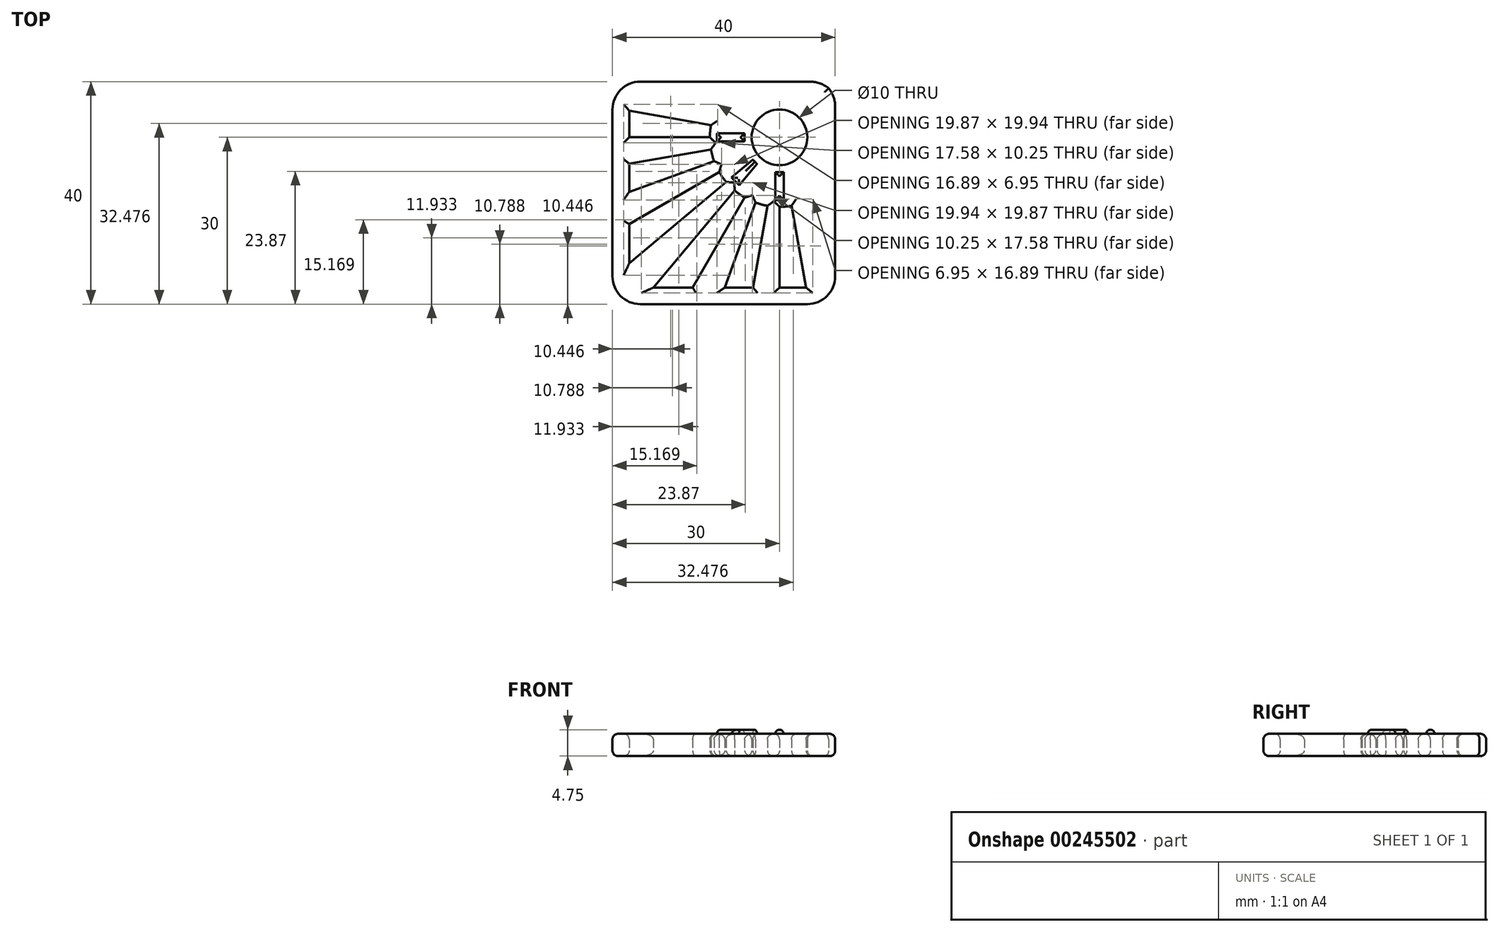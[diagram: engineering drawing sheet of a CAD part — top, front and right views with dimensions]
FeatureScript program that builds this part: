
annotation { "Feature Type Name" : "Feature", "Feature Type Description" : "" }
export const myFeature = defineFeature(function(context is Context, id is Id, definition is map)
    precondition{}
    {
        {
            var Q0;
            Q0=qCreatedBy(makeId("Top.planeOp"),FACE);
            var sketch = newSketch(context, id + "F0", { "sketchPlane" : qUnion([Q0])});
            skLineSegment(sketch, "E0.bottom", {"start": v(0, 0) * mm, "end": v(-40, 0) * mm});
            skLineSegment(sketch, "E0.top", {"start": v(0, -40) * mm, "end": v(-40, -40) * mm});
            skLineSegment(sketch, "E0.left", {"start": v(0, 0) * mm, "end": v(0, -40) * mm});
            skLineSegment(sketch, "E0.right", {"start": v(-40, 0) * mm, "end": v(-40, -40) * mm});
            skPoint(sketch, "E1", {"position": v(-10, -10) * mm});
            skLineSegment(sketch, "E2", {"start": v(-10, -10) * mm, "end": v(-35, -10) * mm});
            skLineSegment(sketch, "E3", {"start": v(-10, -10) * mm, "end": v(-34.62, -5.66) * mm});
            skLineSegment(sketch, "E4", {"start": v(-10, -10) * mm, "end": v(-5.66, -34.62) * mm});
            skLineSegment(sketch, "E5", {"start": v(-10, -10) * mm, "end": v(-10, -35) * mm});
            skLineSegment(sketch, "E6", {"start": v(-10, -10) * mm, "end": v(-34.62, -14.34) * mm});
            skLineSegment(sketch, "E7", {"start": v(-10, -10) * mm, "end": v(-33.5, -18.55) * mm});
            skLineSegment(sketch, "E8", {"start": v(-10, -10) * mm, "end": v(-31.65, -22.5) * mm});
            skLineSegment(sketch, "E9", {"start": v(-10, -10) * mm, "end": v(-29.15, -26.07) * mm});
            skLineSegment(sketch, "E10", {"start": v(-10, -10) * mm, "end": v(-26.07, -29.15) * mm});
            skLineSegment(sketch, "E11", {"start": v(-10, -10) * mm, "end": v(-22.5, -31.65) * mm});
            skLineSegment(sketch, "E12", {"start": v(-10, -10) * mm, "end": v(-18.55, -33.5) * mm});
            skLineSegment(sketch, "E13", {"start": v(-10, -10) * mm, "end": v(-14.34, -34.62) * mm});
            skCircle(sketch, "E14", {"center": v(-10, -10) * mm, "radius": 5 * mm});
            skCircle(sketch, "E15", {"center": v(-10, -10) * mm, "radius": 12.5 * mm});
            skLineSegment(sketch, "E16", {"start": v(-37, -5.24) * mm, "end": v(-37, -37) * mm});
            skLineSegment(sketch, "E17", {"start": v(-37, -37) * mm, "end": v(-5.24, -37) * mm});
            skLineSegment(sketch, "E18", {"start": v(-34.62, -5.66) * mm, "end": v(-37, -5.24) * mm});
            skLineSegment(sketch, "E19", {"start": v(-35, -10) * mm, "end": v(-37, -10) * mm});
            skLineSegment(sketch, "E20", {"start": v(-34.62, -14.34) * mm, "end": v(-37, -14.76) * mm});
            skLineSegment(sketch, "E21", {"start": v(-33.5, -18.55) * mm, "end": v(-37, -19.83) * mm});
            skLineSegment(sketch, "E22", {"start": v(-31.65, -22.5) * mm, "end": v(-37, -25.59) * mm});
            skLineSegment(sketch, "E23", {"start": v(-29.15, -26.07) * mm, "end": v(-37, -32.66) * mm});
            skLineSegment(sketch, "E24", {"start": v(-26.07, -29.15) * mm, "end": v(-32.66, -37) * mm});
            skLineSegment(sketch, "E25", {"start": v(-22.5, -31.65) * mm, "end": v(-25.59, -37) * mm});
            skLineSegment(sketch, "E26", {"start": v(-18.55, -33.5) * mm, "end": v(-19.83, -37) * mm});
            skLineSegment(sketch, "E27", {"start": v(-14.34, -34.62) * mm, "end": v(-14.76, -37) * mm});
            skLineSegment(sketch, "E28", {"start": v(-10, -35) * mm, "end": v(-10, -37) * mm});
            skLineSegment(sketch, "E29", {"start": v(-5.66, -34.62) * mm, "end": v(-5.24, -37) * mm});
            skSolve(sketch);
        }
        {
            var Q0;
            {var subQ0=sQuery(id+"F0.wireOp",EDGE,"E14");var subQ1=sQuery(id+"F0.wireOp",EDGE,"E3");var subQ2=makeQuery(id+"F0.imprint","INTERSECT",VERTEX,{"derivedFrom":[subQ1,subQ0]});Q0=makeQuery(id+"F0.imprint","IMPRINT",FACE,{"disambiguationData":[TD([[makeQuery(id+"F0.imprint","IMPRINT",EDGE,{"disambiguationData":[TD([[subQ2,-1.0]])],"derivedFrom":subQ1}),-1.0]])]});}
            var Q1;
            {var subQ0=sQuery(id+"F0.wireOp",EDGE,"E14");var subQ1=sQuery(id+"F0.wireOp",EDGE,"E4");var subQ2=makeQuery(id+"F0.imprint","INTERSECT",VERTEX,{"derivedFrom":[subQ1,subQ0]});Q1=makeQuery(id+"F0.imprint","IMPRINT",FACE,{"disambiguationData":[TD([[makeQuery(id+"F0.imprint","IMPRINT",EDGE,{"disambiguationData":[TD([[subQ2,-1.0]])],"derivedFrom":subQ1}),-1.0]])]});}
            var Q2;
            {var subQ0=sQuery(id+"F0.wireOp",EDGE,"E14");var subQ1=sQuery(id+"F0.wireOp",EDGE,"E5");var subQ2=makeQuery(id+"F0.imprint","INTERSECT",VERTEX,{"derivedFrom":[subQ1,subQ0]});Q2=makeQuery(id+"F0.imprint","IMPRINT",FACE,{"disambiguationData":[TD([[makeQuery(id+"F0.imprint","IMPRINT",EDGE,{"disambiguationData":[TD([[subQ2,-1.0]])],"derivedFrom":subQ1}),-1.0]])]});}
            var Q3;
            {var subQ0=sQuery(id+"F0.wireOp",EDGE,"E5");var subQ1=sQuery(id+"F0.wireOp",EDGE,"7b7e5d17-fbf7-4574-848a-6fc9f2fd8215.0");var subQ2=makeQuery(id+"F0.imprint","INTERSECT",VERTEX,{"derivedFrom":[subQ1,subQ0]});Q3=makeQuery(id+"F0.imprint","IMPRINT",FACE,{"disambiguationData":[TD([[makeQuery(id+"F0.imprint","IMPRINT",EDGE,{"disambiguationData":[TD([[subQ2,1.0]])],"derivedFrom":subQ1}),1.0]])]});}
            var Q4;
            {var subQ0=sQuery(id+"F0.wireOp",EDGE,"E11");var subQ1=sQuery(id+"F0.wireOp",EDGE,"7b7e5d17-fbf7-4574-848a-6fc9f2fd8215.0");var subQ2=makeQuery(id+"F0.imprint","INTERSECT",VERTEX,{"derivedFrom":[subQ1,subQ0]});Q4=makeQuery(id+"F0.imprint","IMPRINT",FACE,{"disambiguationData":[TD([[makeQuery(id+"F0.imprint","IMPRINT",EDGE,{"disambiguationData":[TD([[subQ2,-1.0]])],"derivedFrom":subQ1}),1.0]])]});}
            var Q5;
            {var subQ0=sQuery(id+"F0.wireOp",EDGE,"E9");var subQ1=sQuery(id+"F0.wireOp",EDGE,"7b7e5d17-fbf7-4574-848a-6fc9f2fd8215.0");var subQ2=makeQuery(id+"F0.imprint","INTERSECT",VERTEX,{"derivedFrom":[subQ1,subQ0]});Q5=makeQuery(id+"F0.imprint","IMPRINT",FACE,{"disambiguationData":[TD([[makeQuery(id+"F0.imprint","IMPRINT",EDGE,{"disambiguationData":[TD([[subQ2,-1.0]])],"derivedFrom":subQ1}),1.0]])]});}
            var Q6;
            {var subQ0=sQuery(id+"F0.wireOp",EDGE,"E7");var subQ1=sQuery(id+"F0.wireOp",EDGE,"7b7e5d17-fbf7-4574-848a-6fc9f2fd8215.0");var subQ2=makeQuery(id+"F0.imprint","INTERSECT",VERTEX,{"derivedFrom":[subQ1,subQ0]});Q6=makeQuery(id+"F0.imprint","IMPRINT",FACE,{"disambiguationData":[TD([[makeQuery(id+"F0.imprint","IMPRINT",EDGE,{"disambiguationData":[TD([[subQ2,-1.0]])],"derivedFrom":subQ1}),1.0]])]});}
            var Q7;
            {var subQ0=sQuery(id+"F0.wireOp",EDGE,"E2");var subQ1=sQuery(id+"F0.wireOp",EDGE,"7b7e5d17-fbf7-4574-848a-6fc9f2fd8215.0");var subQ2=makeQuery(id+"F0.imprint","INTERSECT",VERTEX,{"derivedFrom":[subQ1,subQ0]});Q7=makeQuery(id+"F0.imprint","IMPRINT",FACE,{"disambiguationData":[TD([[makeQuery(id+"F0.imprint","IMPRINT",EDGE,{"disambiguationData":[TD([[subQ2,-1.0]])],"derivedFrom":subQ1}),1.0]])]});}
            var Q8;
            {var subQ0=sQuery(id+"F0.wireOp",EDGE,"E14");var subQ1=sQuery(id+"F0.wireOp",EDGE,"E2");var subQ2=makeQuery(id+"F0.imprint","INTERSECT",VERTEX,{"derivedFrom":[subQ1,subQ0]});Q8=makeQuery(id+"F0.imprint","IMPRINT",FACE,{"disambiguationData":[TD([[makeQuery(id+"F0.imprint","IMPRINT",EDGE,{"disambiguationData":[TD([[subQ2,-1.0]])],"derivedFrom":subQ1}),-1.0]])]});}
            var Q9;
            {var subQ0=sQuery(id+"F0.wireOp",EDGE,"E14");var subQ1=sQuery(id+"F0.wireOp",EDGE,"E2");var subQ2=makeQuery(id+"F0.imprint","INTERSECT",VERTEX,{"derivedFrom":[subQ1,subQ0]});Q9=makeQuery(id+"F0.imprint","IMPRINT",FACE,{"disambiguationData":[TD([[makeQuery(id+"F0.imprint","IMPRINT",EDGE,{"disambiguationData":[TD([[subQ2,-1.0]])],"derivedFrom":subQ1}),1.0]])]});}
            var Q10;
            {var subQ0=sQuery(id+"F0.wireOp",EDGE,"E14");var subQ1=sQuery(id+"F0.wireOp",EDGE,"E6");var subQ2=makeQuery(id+"F0.imprint","INTERSECT",VERTEX,{"derivedFrom":[subQ1,subQ0]});Q10=makeQuery(id+"F0.imprint","IMPRINT",FACE,{"disambiguationData":[TD([[makeQuery(id+"F0.imprint","IMPRINT",EDGE,{"disambiguationData":[TD([[subQ2,-1.0]])],"derivedFrom":subQ1}),1.0]])]});}
            var Q11;
            {var subQ0=sQuery(id+"F0.wireOp",EDGE,"E14");var subQ1=sQuery(id+"F0.wireOp",EDGE,"E7");var subQ2=makeQuery(id+"F0.imprint","INTERSECT",VERTEX,{"derivedFrom":[subQ1,subQ0]});Q11=makeQuery(id+"F0.imprint","IMPRINT",FACE,{"disambiguationData":[TD([[makeQuery(id+"F0.imprint","IMPRINT",EDGE,{"disambiguationData":[TD([[subQ2,-1.0]])],"derivedFrom":subQ1}),1.0]])]});}
            var Q12;
            {var subQ0=sQuery(id+"F0.wireOp",EDGE,"E14");var subQ1=sQuery(id+"F0.wireOp",EDGE,"E8");var subQ2=makeQuery(id+"F0.imprint","INTERSECT",VERTEX,{"derivedFrom":[subQ1,subQ0]});Q12=makeQuery(id+"F0.imprint","IMPRINT",FACE,{"disambiguationData":[TD([[makeQuery(id+"F0.imprint","IMPRINT",EDGE,{"disambiguationData":[TD([[subQ2,-1.0]])],"derivedFrom":subQ1}),1.0]])]});}
            var Q13;
            {var subQ0=sQuery(id+"F0.wireOp",EDGE,"E14");var subQ1=sQuery(id+"F0.wireOp",EDGE,"E9");var subQ2=makeQuery(id+"F0.imprint","INTERSECT",VERTEX,{"derivedFrom":[subQ1,subQ0]});Q13=makeQuery(id+"F0.imprint","IMPRINT",FACE,{"disambiguationData":[TD([[makeQuery(id+"F0.imprint","IMPRINT",EDGE,{"disambiguationData":[TD([[subQ2,-1.0]])],"derivedFrom":subQ1}),1.0]])]});}
            var Q14;
            {var subQ0=sQuery(id+"F0.wireOp",EDGE,"E14");var subQ1=sQuery(id+"F0.wireOp",EDGE,"E10");var subQ2=makeQuery(id+"F0.imprint","INTERSECT",VERTEX,{"derivedFrom":[subQ1,subQ0]});Q14=makeQuery(id+"F0.imprint","IMPRINT",FACE,{"disambiguationData":[TD([[makeQuery(id+"F0.imprint","IMPRINT",EDGE,{"disambiguationData":[TD([[subQ2,-1.0]])],"derivedFrom":subQ1}),1.0]])]});}
            var Q15;
            {var subQ0=sQuery(id+"F0.wireOp",EDGE,"E14");var subQ1=sQuery(id+"F0.wireOp",EDGE,"E11");var subQ2=makeQuery(id+"F0.imprint","INTERSECT",VERTEX,{"derivedFrom":[subQ1,subQ0]});Q15=makeQuery(id+"F0.imprint","IMPRINT",FACE,{"disambiguationData":[TD([[makeQuery(id+"F0.imprint","IMPRINT",EDGE,{"disambiguationData":[TD([[subQ2,-1.0]])],"derivedFrom":subQ1}),1.0]])]});}
            var Q16;
            {var subQ0=sQuery(id+"F0.wireOp",EDGE,"E14");var subQ1=sQuery(id+"F0.wireOp",EDGE,"E12");var subQ2=makeQuery(id+"F0.imprint","INTERSECT",VERTEX,{"derivedFrom":[subQ1,subQ0]});Q16=makeQuery(id+"F0.imprint","IMPRINT",FACE,{"disambiguationData":[TD([[makeQuery(id+"F0.imprint","IMPRINT",EDGE,{"disambiguationData":[TD([[subQ2,-1.0]])],"derivedFrom":subQ1}),1.0]])]});}
            var Q17;
            {var subQ13=sQuery(id+"F0.wireOp",EDGE,"E0.top");Q17=makeQuery(id+"F0.imprint","IMPRINT",FACE,{"disambiguationData":[TD([[makeQuery(id+"F0.imprint","IMPRINT",EDGE,{"derivedFrom":subQ13}),-1.0]])]});}
            var Q18;
            {var subQ5=sQuery(id+"F0.wireOp",EDGE,"E27");Q18=makeQuery(id+"F0.imprint","IMPRINT",FACE,{"disambiguationData":[TD([[makeQuery(id+"F0.imprint","IMPRINT",EDGE,{"derivedFrom":subQ5}),1.0]])]});}
            var Q19;
            {var subQ4=sQuery(id+"F0.wireOp",EDGE,"E25");Q19=makeQuery(id+"F0.imprint","IMPRINT",FACE,{"disambiguationData":[TD([[makeQuery(id+"F0.imprint","IMPRINT",EDGE,{"derivedFrom":subQ4}),1.0]])]});}
            var Q20;
            {var subQ9=sQuery(id+"F0.wireOp",EDGE,"E23");Q20=makeQuery(id+"F0.imprint","IMPRINT",FACE,{"disambiguationData":[TD([[makeQuery(id+"F0.imprint","IMPRINT",EDGE,{"derivedFrom":subQ9}),1.0]])]});}
            var Q21;
            {var subQ5=sQuery(id+"F0.wireOp",EDGE,"E21");Q21=makeQuery(id+"F0.imprint","IMPRINT",FACE,{"disambiguationData":[TD([[makeQuery(id+"F0.imprint","IMPRINT",EDGE,{"derivedFrom":subQ5}),1.0]])]});}
            var Q22;
            {var subQ0=sQuery(id+"F0.wireOp",EDGE,"E19");Q22=makeQuery(id+"F0.imprint","IMPRINT",FACE,{"disambiguationData":[TD([[makeQuery(id+"F0.imprint","IMPRINT",EDGE,{"derivedFrom":subQ0}),1.0]])]});}
            extrude(context, id + "F1", {"entities" : qUnion([Q0, Q1, Q2, Q3, Q4, Q5, Q6, Q7, Q8, Q9, Q10, Q11, Q12, Q13, Q14, Q15, Q16, Q17, Q18, Q19, Q20, Q21, Q22]), "depth" : 4 * mm});
        }
        {
            var Q0;
            Q0=makeQuery(id+"F1.opExtrude","SWEPT_EDGE",EDGE,{"disambiguationData":[OSD([sQuery(id+"F0.wireOp",EDGE,"E0.bottom"),sQuery(id+"F0.wireOp",EDGE,"E0.left")])]});
            var Q1;
            Q1=makeQuery(id+"F1.opExtrude","SWEPT_EDGE",EDGE,{"disambiguationData":[OSD([sQuery(id+"F0.wireOp",EDGE,"E0.top"),sQuery(id+"F0.wireOp",EDGE,"E0.left")])]});
            var Q2;
            Q2=makeQuery(id+"F1.opExtrude","SWEPT_EDGE",EDGE,{"disambiguationData":[OSD([sQuery(id+"F0.wireOp",EDGE,"E0.bottom"),sQuery(id+"F0.wireOp",EDGE,"E0.right")])]});
            var Q3;
            Q3=makeQuery(id+"F1.opExtrude","SWEPT_EDGE",EDGE,{"disambiguationData":[OSD([sQuery(id+"F0.wireOp",EDGE,"E0.top"),sQuery(id+"F0.wireOp",EDGE,"E0.right")])]});
            fillet(context, id + "F2", {"entities" : qUnion([Q0, Q1, Q2, Q3]), "radius" : 5 * mm, "tangentPropagation" : true, "allowEdgeOverflow" : false});
        }
        {
            var Q0;
            Q0=makeQuery(id+"F1.opExtrude","CAP_FACE",FACE,{"disambiguationData":[OSD([sQuery(id+"F0.wireOp",EDGE,"E0.bottom"),sQuery(id+"F0.wireOp",EDGE,"E0.top"),sQuery(id+"F0.wireOp",EDGE,"E0.left"),sQuery(id+"F0.wireOp",EDGE,"E0.right"),sQuery(id+"F0.wireOp",EDGE,"E2"),sQuery(id+"F0.wireOp",EDGE,"E3"),sQuery(id+"F0.wireOp",EDGE,"E4"),sQuery(id+"F0.wireOp",EDGE,"E5"),sQuery(id+"F0.wireOp",EDGE,"E6"),sQuery(id+"F0.wireOp",EDGE,"E7"),sQuery(id+"F0.wireOp",EDGE,"E8"),sQuery(id+"F0.wireOp",EDGE,"E9"),sQuery(id+"F0.wireOp",EDGE,"E10"),sQuery(id+"F0.wireOp",EDGE,"E11"),sQuery(id+"F0.wireOp",EDGE,"E12"),sQuery(id+"F0.wireOp",EDGE,"E13"),sQuery(id+"F0.wireOp",EDGE,"E14"),sQuery(id+"F0.wireOp",EDGE,"E15"),sQuery(id+"F0.wireOp",EDGE,"E16"),sQuery(id+"F0.wireOp",EDGE,"E17"),sQuery(id+"F0.wireOp",EDGE,"E18"),sQuery(id+"F0.wireOp",EDGE,"E19"),sQuery(id+"F0.wireOp",EDGE,"E20"),sQuery(id+"F0.wireOp",EDGE,"E21"),sQuery(id+"F0.wireOp",EDGE,"E22"),sQuery(id+"F0.wireOp",EDGE,"E23"),sQuery(id+"F0.wireOp",EDGE,"E24"),sQuery(id+"F0.wireOp",EDGE,"E25"),sQuery(id+"F0.wireOp",EDGE,"E26"),sQuery(id+"F0.wireOp",EDGE,"E27"),sQuery(id+"F0.wireOp",EDGE,"E28"),sQuery(id+"F0.wireOp",EDGE,"E29")])],"isStart":false});
            var sketch = newSketch(context, id + "F3", { "sketchPlane" : qUnion([Q0])});
            skLineSegment(sketch, "E30", {"start": v(-10, -22.5) * mm, "end": v(-10, -15) * mm});
            skLineSegment(sketch, "E31", {"start": v(-22.5, -10) * mm, "end": v(-15, -10) * mm});
            skLineSegment(sketch, "E32.bottom", {"start": v(-9.25, -21.25) * mm, "end": v(-10.75, -21.25) * mm});
            skLineSegment(sketch, "E32.top", {"start": v(-9.25, -16.25) * mm, "end": v(-10.75, -16.25) * mm});
            skLineSegment(sketch, "E32.left", {"start": v(-9.25, -21.25) * mm, "end": v(-9.25, -16.25) * mm});
            skLineSegment(sketch, "E32.right", {"start": v(-10.75, -21.25) * mm, "end": v(-10.75, -16.25) * mm});
            skPoint(sketch, "E32.middle", {"position": v(-10, -18.75) * mm});
            skLineSegment(sketch, "E33.bottom", {"start": v(-16.25, -10.75) * mm, "end": v(-21.25, -10.75) * mm});
            skLineSegment(sketch, "E33.top", {"start": v(-16.25, -9.25) * mm, "end": v(-21.25, -9.25) * mm});
            skLineSegment(sketch, "E33.left", {"start": v(-16.25, -10.75) * mm, "end": v(-16.25, -9.25) * mm});
            skLineSegment(sketch, "E33.right", {"start": v(-21.25, -10.75) * mm, "end": v(-21.25, -9.25) * mm});
            skPoint(sketch, "E33.middle", {"position": v(-18.75, -10) * mm});
            skLineSegment(sketch, "E34", {"start": v(-19.58, -18.03) * mm, "end": v(-13.83, -13.21) * mm});
            skLineSegment(sketch, "E35", {"start": v(-19.58, -18.03) * mm, "end": v(-18.03, -19.58) * mm});
            skLineSegment(sketch, "E36", {"start": v(-18.03, -19.58) * mm, "end": v(-13.21, -13.83) * mm});
            skLineSegment(sketch, "E37", {"start": v(-14.79, -14.02) * mm, "end": v(-14.02, -14.79) * mm});
            skLineSegment(sketch, "E38", {"start": v(-18.62, -17.23) * mm, "end": v(-17.23, -18.62) * mm});
            skSolve(sketch);
        }
        {
            var Q0;
            {var subQ0=sQuery(id+"F3.wireOp",EDGE,"E37");Q0=makeQuery(id+"F3.imprint","IMPRINT",FACE,{"disambiguationData":[TD([[makeQuery(id+"F3.imprint","IMPRINT",EDGE,{"derivedFrom":subQ0}),-1.0]])]});}
            var Q1;
            {var subQ5=sQuery(id+"F3.wireOp",EDGE,"E32.right");Q1=makeQuery(id+"F3.imprint","IMPRINT",FACE,{"disambiguationData":[TD([[makeQuery(id+"F3.imprint","IMPRINT",EDGE,{"derivedFrom":subQ5}),-1.0]])]});}
            var Q2;
            {var subQ5=sQuery(id+"F3.wireOp",EDGE,"E32.left");Q2=makeQuery(id+"F3.imprint","IMPRINT",FACE,{"disambiguationData":[TD([[makeQuery(id+"F3.imprint","IMPRINT",EDGE,{"derivedFrom":subQ5}),1.0]])]});}
            var Q3;
            {var subQ5=sQuery(id+"F3.wireOp",EDGE,"E33.bottom");Q3=makeQuery(id+"F3.imprint","IMPRINT",FACE,{"disambiguationData":[TD([[makeQuery(id+"F3.imprint","IMPRINT",EDGE,{"derivedFrom":subQ5}),-1.0]])]});}
            var Q4;
            {var subQ5=sQuery(id+"F3.wireOp",EDGE,"E33.top");Q4=makeQuery(id+"F3.imprint","IMPRINT",FACE,{"disambiguationData":[TD([[makeQuery(id+"F3.imprint","IMPRINT",EDGE,{"derivedFrom":subQ5}),1.0]])]});}
            extrude(context, id + "F4", {"entities" : qUnion([Q0, Q1, Q2, Q3, Q4]), "operationType" : NewBodyOperationType.ADD, "depth" : 0.75 * mm});
        }
        {
            var Q0;
            Q0=makeQuery(id+"F4.opExtrude","CAP_EDGE",EDGE,{"disambiguationData":[OSD([sQuery(id+"F3.wireOp",EDGE,"E32.left")])],"isStart":false});
            var Q1;
            Q1=makeQuery(id+"F4.opExtrude","CAP_EDGE",EDGE,{"disambiguationData":[OSD([sQuery(id+"F3.wireOp",EDGE,"E32.right")])],"isStart":false});
            var Q2;
            Q2=makeQuery(id+"F4.opExtrude","CAP_EDGE",EDGE,{"disambiguationData":[OSD([sQuery(id+"F3.wireOp",EDGE,"E36")])],"isStart":false});
            var Q3;
            Q3=makeQuery(id+"F4.opExtrude","CAP_EDGE",EDGE,{"disambiguationData":[OSD([sQuery(id+"F3.wireOp",EDGE,"E34")])],"isStart":false});
            var Q4;
            Q4=makeQuery(id+"F4.opExtrude","CAP_EDGE",EDGE,{"disambiguationData":[OSD([sQuery(id+"F3.wireOp",EDGE,"E33.bottom")])],"isStart":false});
            var Q5;
            Q5=makeQuery(id+"F4.opExtrude","CAP_EDGE",EDGE,{"disambiguationData":[OSD([sQuery(id+"F3.wireOp",EDGE,"E33.top")])],"isStart":false});
            var Q6;
            Q6=makeQuery(id+"F4.opExtrude","CAP_EDGE",EDGE,{"disambiguationData":[OSD([sQuery(id+"F3.wireOp",EDGE,"E38")])],"isStart":false});
            var Q7;
            Q7=makeQuery(id+"F4.opExtrude","CAP_EDGE",EDGE,{"disambiguationData":[OSD([sQuery(id+"F3.wireOp",EDGE,"E32.bottom")])],"isStart":false});
            var Q8;
            Q8=makeQuery(id+"F4.opExtrude","CAP_EDGE",EDGE,{"disambiguationData":[OSD([sQuery(id+"F3.wireOp",EDGE,"E33.right")])],"isStart":false});
            var Q9;
            Q9=makeQuery(id+"F4.opExtrude","CAP_EDGE",EDGE,{"disambiguationData":[OSD([sQuery(id+"F3.wireOp",EDGE,"E33.left")])],"isStart":false});
            var Q10;
            Q10=makeQuery(id+"F4.opExtrude","CAP_EDGE",EDGE,{"disambiguationData":[OSD([sQuery(id+"F3.wireOp",EDGE,"E37")])],"isStart":false});
            var Q11;
            Q11=makeQuery(id+"F4.opExtrude","CAP_EDGE",EDGE,{"disambiguationData":[OSD([sQuery(id+"F3.wireOp",EDGE,"E32.top")])],"isStart":false});
            fillet(context, id + "F5", {"entities" : qUnion([Q0, Q1, Q2, Q3, Q4, Q5, Q6, Q7, Q8, Q9, Q10, Q11]), "radius" : 0.75 * mm, "tangentPropagation" : true, "allowEdgeOverflow" : false});
        }
        {
            var Q0;
            Q0=makeQuery(id+"F1.opExtrude","CAP_EDGE",EDGE,{"disambiguationData":[OSD([sQuery(id+"F0.wireOp",EDGE,"E4"),sQuery(id+"F0.wireOp",EDGE,"E29")])],"isStart":false});
            var Q1;
            {var subQ0=sQuery(id+"F0.wireOp",EDGE,"E15");Q1=makeQuery(id+"F1.opExtrude","CAP_EDGE",EDGE,{"disambiguationData":[OSD([subQ0]),TDD([makeQuery(id+"F0.imprint","IMPRINT",EDGE,{"disambiguationData":[TD([[makeQuery(id+"F0.imprint","INTERSECT",VERTEX,{"derivedFrom":[sQuery(id+"F0.wireOp",EDGE,"E4"),subQ0]}),1.0]])],"derivedFrom":subQ0})])],"isStart":false});}
            var Q2;
            Q2=makeQuery(id+"F1.opExtrude","CAP_EDGE",EDGE,{"disambiguationData":[OSD([sQuery(id+"F0.wireOp",EDGE,"E5"),sQuery(id+"F0.wireOp",EDGE,"E28")])],"isStart":false});
            var Q3;
            {var subQ0=sQuery(id+"F0.wireOp",EDGE,"E17");Q3=makeQuery(id+"F1.opExtrude","CAP_EDGE",EDGE,{"disambiguationData":[OSD([subQ0]),TDD([makeQuery(id+"F0.imprint","IMPRINT",EDGE,{"disambiguationData":[TD([[makeQuery(id+"F0.imprint","INTERSECT",VERTEX,{"derivedFrom":[subQ0,sQuery(id+"F0.wireOp",EDGE,"E29")]}),1.0]])],"derivedFrom":subQ0})])],"isStart":false});}
            var Q4;
            Q4=makeQuery(id+"F1.opExtrude","CAP_EDGE",EDGE,{"disambiguationData":[OSD([sQuery(id+"F0.wireOp",EDGE,"E13"),sQuery(id+"F0.wireOp",EDGE,"E27")])],"isStart":false});
            var Q5;
            {var subQ0=sQuery(id+"F0.wireOp",EDGE,"E17");Q5=makeQuery(id+"F1.opExtrude","CAP_EDGE",EDGE,{"disambiguationData":[OSD([subQ0]),TDD([makeQuery(id+"F0.imprint","IMPRINT",EDGE,{"disambiguationData":[TD([[makeQuery(id+"F0.imprint","INTERSECT",VERTEX,{"derivedFrom":[subQ0,sQuery(id+"F0.wireOp",EDGE,"E26")]}),-1.0]])],"derivedFrom":subQ0})])],"isStart":false});}
            var Q6;
            Q6=makeQuery(id+"F1.opExtrude","CAP_EDGE",EDGE,{"disambiguationData":[OSD([sQuery(id+"F0.wireOp",EDGE,"E12"),sQuery(id+"F0.wireOp",EDGE,"E26")])],"isStart":false});
            var Q7;
            {var subQ0=sQuery(id+"F0.wireOp",EDGE,"E15");Q7=makeQuery(id+"F1.opExtrude","CAP_EDGE",EDGE,{"disambiguationData":[OSD([subQ0]),TDD([makeQuery(id+"F0.imprint","IMPRINT",EDGE,{"disambiguationData":[TD([[makeQuery(id+"F0.imprint","INTERSECT",VERTEX,{"derivedFrom":[sQuery(id+"F0.wireOp",EDGE,"E12"),subQ0]}),-1.0]])],"derivedFrom":subQ0})])],"isStart":false});}
            var Q8;
            Q8=makeQuery(id+"F1.opExtrude","CAP_EDGE",EDGE,{"disambiguationData":[OSD([sQuery(id+"F0.wireOp",EDGE,"E11"),sQuery(id+"F0.wireOp",EDGE,"E25")])],"isStart":false});
            var Q9;
            {var subQ0=sQuery(id+"F0.wireOp",EDGE,"E15");Q9=makeQuery(id+"F1.opExtrude","CAP_EDGE",EDGE,{"disambiguationData":[OSD([subQ0]),TDD([makeQuery(id+"F0.imprint","IMPRINT",EDGE,{"disambiguationData":[TD([[makeQuery(id+"F0.imprint","INTERSECT",VERTEX,{"derivedFrom":[sQuery(id+"F0.wireOp",EDGE,"E10"),subQ0]}),-1.0]])],"derivedFrom":subQ0})])],"isStart":false});}
            var Q10;
            Q10=makeQuery(id+"F1.opExtrude","CAP_EDGE",EDGE,{"disambiguationData":[OSD([sQuery(id+"F0.wireOp",EDGE,"E3"),sQuery(id+"F0.wireOp",EDGE,"E18")])],"isStart":false});
            var Q11;
            {var subQ0=sQuery(id+"F0.wireOp",EDGE,"E16");Q11=makeQuery(id+"F1.opExtrude","CAP_EDGE",EDGE,{"disambiguationData":[OSD([subQ0]),TDD([makeQuery(id+"F0.imprint","IMPRINT",EDGE,{"disambiguationData":[TD([[makeQuery(id+"F0.imprint","INTERSECT",VERTEX,{"derivedFrom":[subQ0,sQuery(id+"F0.wireOp",EDGE,"E18")]}),-1.0]])],"derivedFrom":subQ0})])],"isStart":false});}
            var Q12;
            {var subQ0=sQuery(id+"F0.wireOp",EDGE,"E16");Q12=makeQuery(id+"F1.opExtrude","CAP_EDGE",EDGE,{"disambiguationData":[OSD([subQ0]),TDD([makeQuery(id+"F0.imprint","IMPRINT",EDGE,{"disambiguationData":[TD([[makeQuery(id+"F0.imprint","INTERSECT",VERTEX,{"derivedFrom":[subQ0,sQuery(id+"F0.wireOp",EDGE,"E20")]}),-1.0]])],"derivedFrom":subQ0})])],"isStart":false});}
            var Q13;
            Q13=makeQuery(id+"F1.opExtrude","CAP_EDGE",EDGE,{"disambiguationData":[OSD([sQuery(id+"F0.wireOp",EDGE,"E2"),sQuery(id+"F0.wireOp",EDGE,"E19")])],"isStart":false});
            var Q14;
            Q14=makeQuery(id+"F1.opExtrude","CAP_EDGE",EDGE,{"disambiguationData":[OSD([sQuery(id+"F0.wireOp",EDGE,"E6"),sQuery(id+"F0.wireOp",EDGE,"E20")])],"isStart":false});
            var Q15;
            {var subQ0=sQuery(id+"F0.wireOp",EDGE,"E15");Q15=makeQuery(id+"F1.opExtrude","CAP_EDGE",EDGE,{"disambiguationData":[OSD([subQ0]),TDD([makeQuery(id+"F0.imprint","IMPRINT",EDGE,{"disambiguationData":[TD([[makeQuery(id+"F0.imprint","INTERSECT",VERTEX,{"derivedFrom":[sQuery(id+"F0.wireOp",EDGE,"E2"),subQ0]}),1.0]])],"derivedFrom":subQ0})])],"isStart":false});}
            var Q16;
            {var subQ0=sQuery(id+"F0.wireOp",EDGE,"E15");Q16=makeQuery(id+"F1.opExtrude","CAP_EDGE",EDGE,{"disambiguationData":[OSD([subQ0]),TDD([makeQuery(id+"F0.imprint","IMPRINT",EDGE,{"disambiguationData":[TD([[makeQuery(id+"F0.imprint","INTERSECT",VERTEX,{"derivedFrom":[sQuery(id+"F0.wireOp",EDGE,"E6"),subQ0]}),-1.0]])],"derivedFrom":subQ0})])],"isStart":false});}
            var Q17;
            Q17=makeQuery(id+"F1.opExtrude","CAP_EDGE",EDGE,{"disambiguationData":[OSD([sQuery(id+"F0.wireOp",EDGE,"E7"),sQuery(id+"F0.wireOp",EDGE,"E21")])],"isStart":false});
            var Q18;
            Q18=makeQuery(id+"F1.opExtrude","CAP_EDGE",EDGE,{"disambiguationData":[OSD([sQuery(id+"F0.wireOp",EDGE,"E8"),sQuery(id+"F0.wireOp",EDGE,"E22")])],"isStart":false});
            var Q19;
            {var subQ0=sQuery(id+"F0.wireOp",EDGE,"E15");Q19=makeQuery(id+"F1.opExtrude","CAP_EDGE",EDGE,{"disambiguationData":[OSD([subQ0]),TDD([makeQuery(id+"F0.imprint","IMPRINT",EDGE,{"disambiguationData":[TD([[makeQuery(id+"F0.imprint","INTERSECT",VERTEX,{"derivedFrom":[sQuery(id+"F0.wireOp",EDGE,"E8"),subQ0]}),-1.0]])],"derivedFrom":subQ0})])],"isStart":false});}
            var Q20;
            {var subQ0=sQuery(id+"F0.wireOp",EDGE,"E16");Q20=makeQuery(id+"F1.opExtrude","CAP_EDGE",EDGE,{"disambiguationData":[OSD([subQ0]),TDD([makeQuery(id+"F0.imprint","IMPRINT",EDGE,{"disambiguationData":[TD([[makeQuery(id+"F0.imprint","INTERSECT",VERTEX,{"derivedFrom":[subQ0,sQuery(id+"F0.wireOp",EDGE,"E22")]}),-1.0]])],"derivedFrom":subQ0})])],"isStart":false});}
            var Q21;
            {var subQ0=sQuery(id+"F0.wireOp",EDGE,"E17");Q21=makeQuery(id+"F1.opExtrude","CAP_EDGE",EDGE,{"disambiguationData":[OSD([subQ0]),TDD([makeQuery(id+"F0.imprint","IMPRINT",EDGE,{"disambiguationData":[TD([[makeQuery(id+"F0.imprint","INTERSECT",VERTEX,{"derivedFrom":[subQ0,sQuery(id+"F0.wireOp",EDGE,"E24")]}),-1.0]])],"derivedFrom":subQ0})])],"isStart":false});}
            var Q22;
            Q22=makeQuery(id+"F1.opExtrude","CAP_EDGE",EDGE,{"disambiguationData":[OSD([sQuery(id+"F0.wireOp",EDGE,"E10"),sQuery(id+"F0.wireOp",EDGE,"E24")])],"isStart":false});
            var Q23;
            Q23=makeQuery(id+"F1.opExtrude","CAP_EDGE",EDGE,{"disambiguationData":[OSD([sQuery(id+"F0.wireOp",EDGE,"E9"),sQuery(id+"F0.wireOp",EDGE,"E23")])],"isStart":false});
            var Q24;
            Q24=makeQuery(id+"F1.opExtrude","CAP_EDGE",EDGE,{"disambiguationData":[OSD([sQuery(id+"F0.wireOp",EDGE,"E14")])],"isStart":false});
            var Q25;
            Q25=makeQuery(id+"F1.opExtrude","CAP_EDGE",EDGE,{"disambiguationData":[OSD([sQuery(id+"F0.wireOp",EDGE,"E0.right")])],"isStart":false});
            var Q26;
            Q26=makeQuery(id+"F1.opExtrude","CAP_EDGE",EDGE,{"disambiguationData":[OSD([sQuery(id+"F0.wireOp",EDGE,"E14")])],"isStart":true});
            var Q27;
            Q27=makeQuery(id+"F1.opExtrude","CAP_EDGE",EDGE,{"disambiguationData":[OSD([sQuery(id+"F0.wireOp",EDGE,"E0.left")])],"isStart":true});
            var Q28;
            Q28=makeQuery(id+"F1.opExtrude","CAP_EDGE",EDGE,{"disambiguationData":[OSD([sQuery(id+"F0.wireOp",EDGE,"E3"),sQuery(id+"F0.wireOp",EDGE,"E18")])],"isStart":true});
            var Q29;
            {var subQ0=sQuery(id+"F0.wireOp",EDGE,"E15");Q29=makeQuery(id+"F1.opExtrude","CAP_EDGE",EDGE,{"disambiguationData":[OSD([subQ0]),TDD([makeQuery(id+"F0.imprint","IMPRINT",EDGE,{"disambiguationData":[TD([[makeQuery(id+"F0.imprint","INTERSECT",VERTEX,{"derivedFrom":[sQuery(id+"F0.wireOp",EDGE,"E2"),subQ0]}),1.0]])],"derivedFrom":subQ0})])],"isStart":true});}
            var Q30;
            {var subQ0=sQuery(id+"F0.wireOp",EDGE,"E16");Q30=makeQuery(id+"F1.opExtrude","CAP_EDGE",EDGE,{"disambiguationData":[OSD([subQ0]),TDD([makeQuery(id+"F0.imprint","IMPRINT",EDGE,{"disambiguationData":[TD([[makeQuery(id+"F0.imprint","INTERSECT",VERTEX,{"derivedFrom":[subQ0,sQuery(id+"F0.wireOp",EDGE,"E18")]}),-1.0]])],"derivedFrom":subQ0})])],"isStart":true});}
            var Q31;
            Q31=makeQuery(id+"F1.opExtrude","CAP_EDGE",EDGE,{"disambiguationData":[OSD([sQuery(id+"F0.wireOp",EDGE,"E2"),sQuery(id+"F0.wireOp",EDGE,"E19")])],"isStart":true});
            var Q32;
            Q32=makeQuery(id+"F1.opExtrude","CAP_EDGE",EDGE,{"disambiguationData":[OSD([sQuery(id+"F0.wireOp",EDGE,"E6"),sQuery(id+"F0.wireOp",EDGE,"E20")])],"isStart":true});
            var Q33;
            {var subQ0=sQuery(id+"F0.wireOp",EDGE,"E16");Q33=makeQuery(id+"F1.opExtrude","CAP_EDGE",EDGE,{"disambiguationData":[OSD([subQ0]),TDD([makeQuery(id+"F0.imprint","IMPRINT",EDGE,{"disambiguationData":[TD([[makeQuery(id+"F0.imprint","INTERSECT",VERTEX,{"derivedFrom":[subQ0,sQuery(id+"F0.wireOp",EDGE,"E20")]}),-1.0]])],"derivedFrom":subQ0})])],"isStart":true});}
            var Q34;
            Q34=makeQuery(id+"F1.opExtrude","CAP_EDGE",EDGE,{"disambiguationData":[OSD([sQuery(id+"F0.wireOp",EDGE,"E7"),sQuery(id+"F0.wireOp",EDGE,"E21")])],"isStart":true});
            var Q35;
            {var subQ0=sQuery(id+"F0.wireOp",EDGE,"E15");Q35=makeQuery(id+"F1.opExtrude","CAP_EDGE",EDGE,{"disambiguationData":[OSD([subQ0]),TDD([makeQuery(id+"F0.imprint","IMPRINT",EDGE,{"disambiguationData":[TD([[makeQuery(id+"F0.imprint","INTERSECT",VERTEX,{"derivedFrom":[sQuery(id+"F0.wireOp",EDGE,"E6"),subQ0]}),-1.0]])],"derivedFrom":subQ0})])],"isStart":true});}
            var Q36;
            Q36=makeQuery(id+"F1.opExtrude","CAP_EDGE",EDGE,{"disambiguationData":[OSD([sQuery(id+"F0.wireOp",EDGE,"E8"),sQuery(id+"F0.wireOp",EDGE,"E22")])],"isStart":true});
            var Q37;
            {var subQ0=sQuery(id+"F0.wireOp",EDGE,"E15");Q37=makeQuery(id+"F1.opExtrude","CAP_EDGE",EDGE,{"disambiguationData":[OSD([subQ0]),TDD([makeQuery(id+"F0.imprint","IMPRINT",EDGE,{"disambiguationData":[TD([[makeQuery(id+"F0.imprint","INTERSECT",VERTEX,{"derivedFrom":[sQuery(id+"F0.wireOp",EDGE,"E8"),subQ0]}),-1.0]])],"derivedFrom":subQ0})])],"isStart":true});}
            var Q38;
            Q38=makeQuery(id+"F1.opExtrude","CAP_EDGE",EDGE,{"disambiguationData":[OSD([sQuery(id+"F0.wireOp",EDGE,"E9"),sQuery(id+"F0.wireOp",EDGE,"E23")])],"isStart":true});
            var Q39;
            {var subQ0=sQuery(id+"F0.wireOp",EDGE,"E15");Q39=makeQuery(id+"F1.opExtrude","CAP_EDGE",EDGE,{"disambiguationData":[OSD([subQ0]),TDD([makeQuery(id+"F0.imprint","IMPRINT",EDGE,{"disambiguationData":[TD([[makeQuery(id+"F0.imprint","INTERSECT",VERTEX,{"derivedFrom":[sQuery(id+"F0.wireOp",EDGE,"E10"),subQ0]}),-1.0]])],"derivedFrom":subQ0})])],"isStart":true});}
            var Q40;
            Q40=makeQuery(id+"F1.opExtrude","CAP_EDGE",EDGE,{"disambiguationData":[OSD([sQuery(id+"F0.wireOp",EDGE,"E10"),sQuery(id+"F0.wireOp",EDGE,"E24")])],"isStart":true});
            var Q41;
            Q41=makeQuery(id+"F1.opExtrude","CAP_EDGE",EDGE,{"disambiguationData":[OSD([sQuery(id+"F0.wireOp",EDGE,"E11"),sQuery(id+"F0.wireOp",EDGE,"E25")])],"isStart":true});
            var Q42;
            {var subQ0=sQuery(id+"F0.wireOp",EDGE,"E16");Q42=makeQuery(id+"F1.opExtrude","CAP_EDGE",EDGE,{"disambiguationData":[OSD([subQ0]),TDD([makeQuery(id+"F0.imprint","IMPRINT",EDGE,{"disambiguationData":[TD([[makeQuery(id+"F0.imprint","INTERSECT",VERTEX,{"derivedFrom":[subQ0,sQuery(id+"F0.wireOp",EDGE,"E22")]}),-1.0]])],"derivedFrom":subQ0})])],"isStart":true});}
            var Q43;
            {var subQ0=sQuery(id+"F0.wireOp",EDGE,"E17");Q43=makeQuery(id+"F1.opExtrude","CAP_EDGE",EDGE,{"disambiguationData":[OSD([subQ0]),TDD([makeQuery(id+"F0.imprint","IMPRINT",EDGE,{"disambiguationData":[TD([[makeQuery(id+"F0.imprint","INTERSECT",VERTEX,{"derivedFrom":[subQ0,sQuery(id+"F0.wireOp",EDGE,"E24")]}),-1.0]])],"derivedFrom":subQ0})])],"isStart":true});}
            var Q44;
            {var subQ0=sQuery(id+"F0.wireOp",EDGE,"E17");Q44=makeQuery(id+"F1.opExtrude","CAP_EDGE",EDGE,{"disambiguationData":[OSD([subQ0]),TDD([makeQuery(id+"F0.imprint","IMPRINT",EDGE,{"disambiguationData":[TD([[makeQuery(id+"F0.imprint","INTERSECT",VERTEX,{"derivedFrom":[subQ0,sQuery(id+"F0.wireOp",EDGE,"E26")]}),-1.0]])],"derivedFrom":subQ0})])],"isStart":true});}
            var Q45;
            {var subQ0=sQuery(id+"F0.wireOp",EDGE,"E17");Q45=makeQuery(id+"F1.opExtrude","CAP_EDGE",EDGE,{"disambiguationData":[OSD([subQ0]),TDD([makeQuery(id+"F0.imprint","IMPRINT",EDGE,{"disambiguationData":[TD([[makeQuery(id+"F0.imprint","INTERSECT",VERTEX,{"derivedFrom":[subQ0,sQuery(id+"F0.wireOp",EDGE,"E29")]}),1.0]])],"derivedFrom":subQ0})])],"isStart":true});}
            var Q46;
            {var subQ0=sQuery(id+"F0.wireOp",EDGE,"E15");Q46=makeQuery(id+"F1.opExtrude","CAP_EDGE",EDGE,{"disambiguationData":[OSD([subQ0]),TDD([makeQuery(id+"F0.imprint","IMPRINT",EDGE,{"disambiguationData":[TD([[makeQuery(id+"F0.imprint","INTERSECT",VERTEX,{"derivedFrom":[sQuery(id+"F0.wireOp",EDGE,"E12"),subQ0]}),-1.0]])],"derivedFrom":subQ0})])],"isStart":true});}
            var Q47;
            {var subQ0=sQuery(id+"F0.wireOp",EDGE,"E15");Q47=makeQuery(id+"F1.opExtrude","CAP_EDGE",EDGE,{"disambiguationData":[OSD([subQ0]),TDD([makeQuery(id+"F0.imprint","IMPRINT",EDGE,{"disambiguationData":[TD([[makeQuery(id+"F0.imprint","INTERSECT",VERTEX,{"derivedFrom":[sQuery(id+"F0.wireOp",EDGE,"E4"),subQ0]}),1.0]])],"derivedFrom":subQ0})])],"isStart":true});}
            var Q48;
            Q48=makeQuery(id+"F1.opExtrude","CAP_EDGE",EDGE,{"disambiguationData":[OSD([sQuery(id+"F0.wireOp",EDGE,"E4"),sQuery(id+"F0.wireOp",EDGE,"E29")])],"isStart":true});
            var Q49;
            Q49=makeQuery(id+"F1.opExtrude","CAP_EDGE",EDGE,{"disambiguationData":[OSD([sQuery(id+"F0.wireOp",EDGE,"E5"),sQuery(id+"F0.wireOp",EDGE,"E28")])],"isStart":true});
            var Q50;
            Q50=makeQuery(id+"F1.opExtrude","CAP_EDGE",EDGE,{"disambiguationData":[OSD([sQuery(id+"F0.wireOp",EDGE,"E13"),sQuery(id+"F0.wireOp",EDGE,"E27")])],"isStart":true});
            var Q51;
            Q51=makeQuery(id+"F1.opExtrude","CAP_EDGE",EDGE,{"disambiguationData":[OSD([sQuery(id+"F0.wireOp",EDGE,"E12"),sQuery(id+"F0.wireOp",EDGE,"E26")])],"isStart":true});
            fillet(context, id + "F6", {"entities" : qUnion([Q0, Q1, Q2, Q3, Q4, Q5, Q6, Q7, Q8, Q9, Q10, Q11, Q12, Q13, Q14, Q15, Q16, Q17, Q18, Q19, Q20, Q21, Q22, Q23, Q24, Q25, Q26, Q27, Q28, Q29, Q30, Q31, Q32, Q33, Q34, Q35, Q36, Q37, Q38, Q39, Q40, Q41, Q42, Q43, Q44, Q45, Q46, Q47, Q48, Q49, Q50, Q51]), "radius" : 1 * mm, "tangentPropagation" : true, "allowEdgeOverflow" : false});
        }
    });
